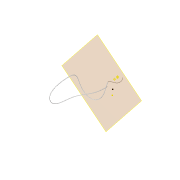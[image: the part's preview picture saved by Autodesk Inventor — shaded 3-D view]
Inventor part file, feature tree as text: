
AUTODESK INVENTOR PART (.ipt)
format: ipt  version: 2022 (Build 260153000, 153)  size: 287,232 bytes
history: native  units: mm
features: other x7, sketch x2, plane x2, sweep x1
ambient origin geometry x8: Origin, YZ Plane, XZ Plane, XY Plane, X Axis, Y Axis, Z Axis, Center Point
bodies: Volumenkörper1 (feature_tree)
feature tree (12):
  other  "3D-Skizze1"
  sketch  "Skizze1"  dims[d0=0.0mm d1=0.0mm]
  plane  "Arbeitsebene2"
  sweep  "Sweeping1"
  other  "Arbeitspunkt1"
  other  "Arbeitspunkt2"
  other  "Arbeitspunkt3"
  plane  "Arbeitsebene1"
  sketch  "Skizze2"
  other  "Anglerfish_bonne_mamman_m12large_flipped_v0.iam"
  other  "00_Coverglass:1"
  other  "Anglerfish_Lightplate_Tosslink_flipped:1"
